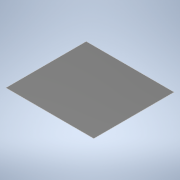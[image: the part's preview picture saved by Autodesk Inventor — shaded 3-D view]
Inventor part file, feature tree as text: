
AUTODESK INVENTOR PART (.ipt)
format: ipt  version: 2022 (Build 260153000, 153)  size: 92,672 bytes
history: native  units: in
note: dims shown in document units (in); Inventor stores cm internally (conversion verified against a paired STEP export)
features: extrude x1, sketch x1
ambient origin geometry x8: Origin, YZ Plane, XZ Plane, XY Plane, X Axis, Y Axis, Z Axis, Center Point
bodies: Solid1 (feature_tree)
feature tree (2):
  extrude  "Extrusion1"  Depth=1.8346in
  sketch  "Sketch1"  dims[d0=1.6772in d1=1.8346in d2=0.0031in d3=0.0in]
